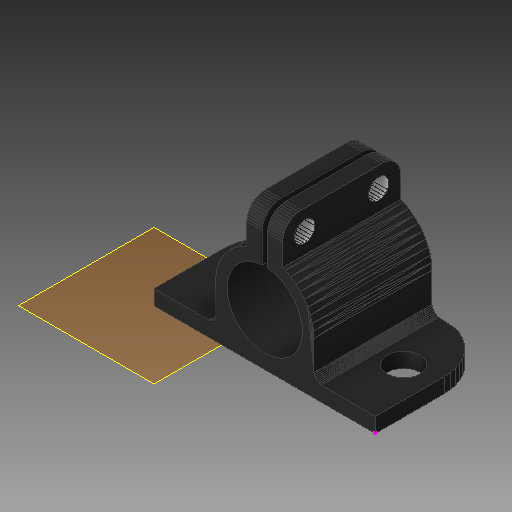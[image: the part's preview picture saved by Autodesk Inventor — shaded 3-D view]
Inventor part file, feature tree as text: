
AUTODESK INVENTOR PART (.ipt)
format: ipt  version: 2018 (Build 220112000, 112)  size: 719,872 bytes
history: native  units: mm
features: sketch x6, other x3, plane x2, hole x1, projected_geometry x1
ambient origin geometry x8: Origin, YZ Plane, XZ Plane, XY Plane, X Axis, Y Axis, Z Axis, Center Point
bodies: Solid1 (feature_tree)
feature tree (13):
  other  "12mmrodholder_CPY.ipt"
  hole  "Hole1"  [1 undecoded]
  other  "Solid1::12mmrodholder_CPY.ipt"
  other  "TaggingFeature1"
  sketch  "Sketch2"  dims[d0=10.0mm]
  sketch  "Sketch3"  dims[d1=3.3mm d2=6.0mm d3=4.0mm d4=2.0mm d5=90.0deg d6=8.0mm d7=20.594885mm]
  sketch  "Sketch4"
  sketch  "Sketch5"
  sketch  "Sketch6"
  plane  "Work Plane1"
  plane  "Work Plane2"
  sketch  "Sketch7"
  projected_geometry  "Projected Loop1"
note: 1 required parameter value undecoded (feature->parameter linkage not recoverable at this tier; creation-order binding heuristic only, values carry confidence <= 0.55)
